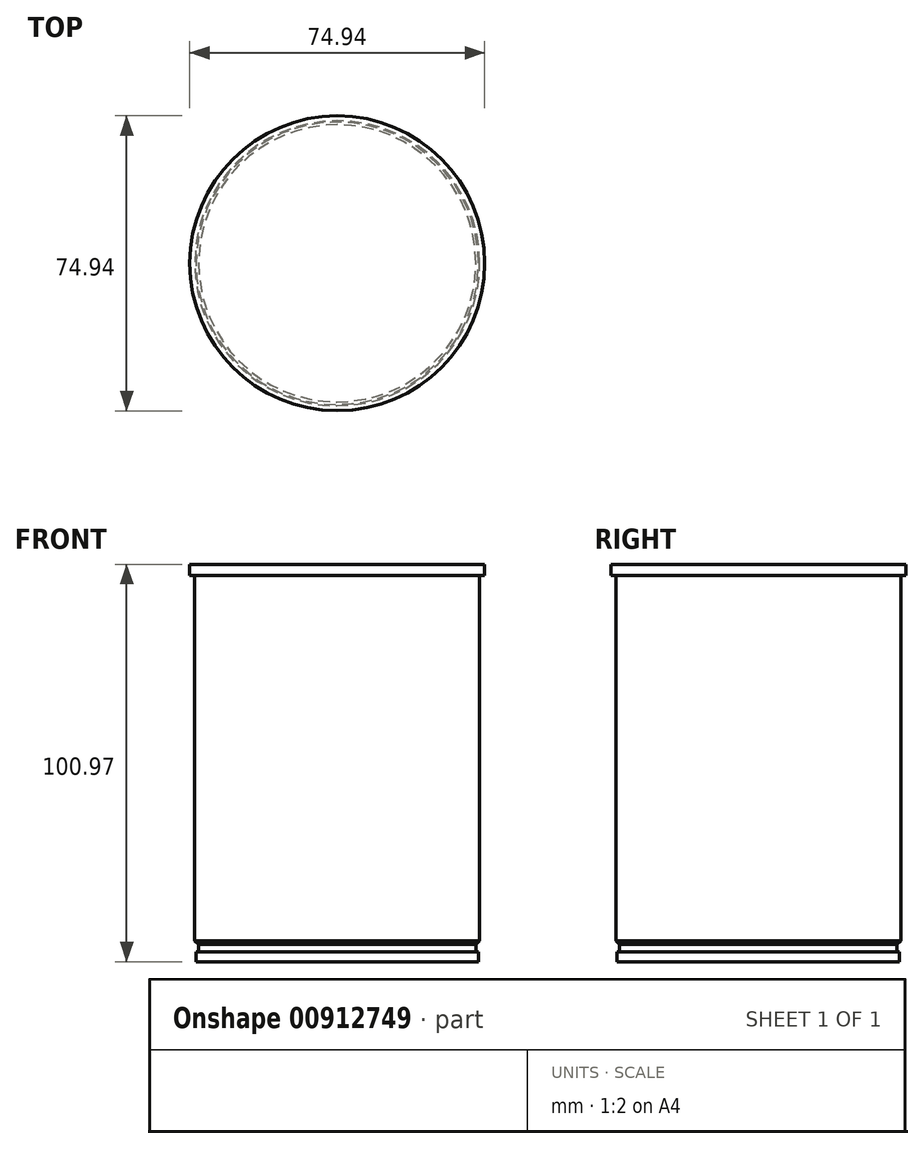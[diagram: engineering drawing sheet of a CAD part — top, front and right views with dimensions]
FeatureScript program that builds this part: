
annotation { "Feature Type Name" : "Feature", "Feature Type Description" : "" }
export const myFeature = defineFeature(function(context is Context, id is Id, definition is map)
    precondition{}
    {
        {
            var Q0;
            Q0=qCreatedBy(makeId("Top.planeOp"),FACE);
            var sketch = newSketch(context, id + "F0", { "sketchPlane" : qUnion([Q0])});
            skCircle(sketch, "E0", {"center": v(0, 0) * mm, "radius": 35.88 * mm});
            skSolve(sketch);
        }
        {
            var Q0;
            Q0=makeQuery(id+"F0.imprint","IMPRINT",FACE,{"disambiguationData":[TD([[makeQuery(id+"F0.imprint","IMPRINT",EDGE,{"derivedFrom":sQuery(id+"F0.wireOp",EDGE,"E0")}),1.0]])]});
            extrude(context, id + "F1", {"entities" : qUnion([Q0]), "depth" : 2.54 * mm, "offsetDistance" : 25.4 * mm});
        }
        {
            var Q0;
            Q0=makeQuery(id+"F1.opExtrude","CAP_FACE",FACE,{"disambiguationData":[OSD([sQuery(id+"F0.wireOp",EDGE,"E0")])],"isStart":false});
            var sketch = newSketch(context, id + "F2", { "sketchPlane" : qUnion([Q0])});
            skCircle(sketch, "E1", {"center": v(0, 0) * mm, "radius": 35.21 * mm});
            skSolve(sketch);
        }
        {
            var Q0;
            Q0 = qSketchRegion(id + "F2", true);
            extrude(context, id + "F3", {"entities" : qUnion([Q0]), "operationType" : NewBodyOperationType.ADD, "depth" : 1.78 * mm, "offsetDistance" : 25.4 * mm});
        }
        {
            var Q0;
            Q0=makeQuery(id+"F3.opExtrude","CAP_FACE",FACE,{"disambiguationData":[OSD([sQuery(id+"F2.wireOp",EDGE,"E1")])],"isStart":false});
            var sketch = newSketch(context, id + "F4", { "sketchPlane" : qUnion([Q0])});
            skCircle(sketch, "E2", {"center": v(0, 0) * mm, "radius": 36.2 * mm});
            skSolve(sketch);
        }
        {
            var Q0;
            Q0 = qSketchRegion(id + "F4", true);
            extrude(context, id + "F5", {"entities" : qUnion([Q0]), "operationType" : NewBodyOperationType.ADD, "depth" : 93.85 * mm, "offsetDistance" : 25.4 * mm});
        }
        {
            var Q0;
            Q0=makeQuery(id+"F5.opExtrude","CAP_FACE",FACE,{"disambiguationData":[OSD([sQuery(id+"F4.wireOp",EDGE,"E2")])],"isStart":false});
            var sketch = newSketch(context, id + "F6", { "sketchPlane" : qUnion([Q0])});
            skCircle(sketch, "E3", {"center": v(0, 0) * mm, "radius": 37.47 * mm});
            skSolve(sketch);
        }
        {
            var Q0;
            Q0 = qSketchRegion(id + "F6", true);
            extrude(context, id + "F7", {"entities" : qUnion([Q0]), "operationType" : NewBodyOperationType.ADD, "depth" : 2.8 * mm, "offsetDistance" : 25.4 * mm});
        }
        {
            var Q0;
            Q0=makeQuery(id+"F5.opExtrude","CAP_EDGE",EDGE,{"disambiguationData":[OSD([sQuery(id+"F4.wireOp",EDGE,"E2")])],"isStart":true});
            chamfer(context, id + "F8", {"entities" : qUnion([Q0]), "width" : 1.02 * mm, "tangentPropagation" : true});
        }
    });
